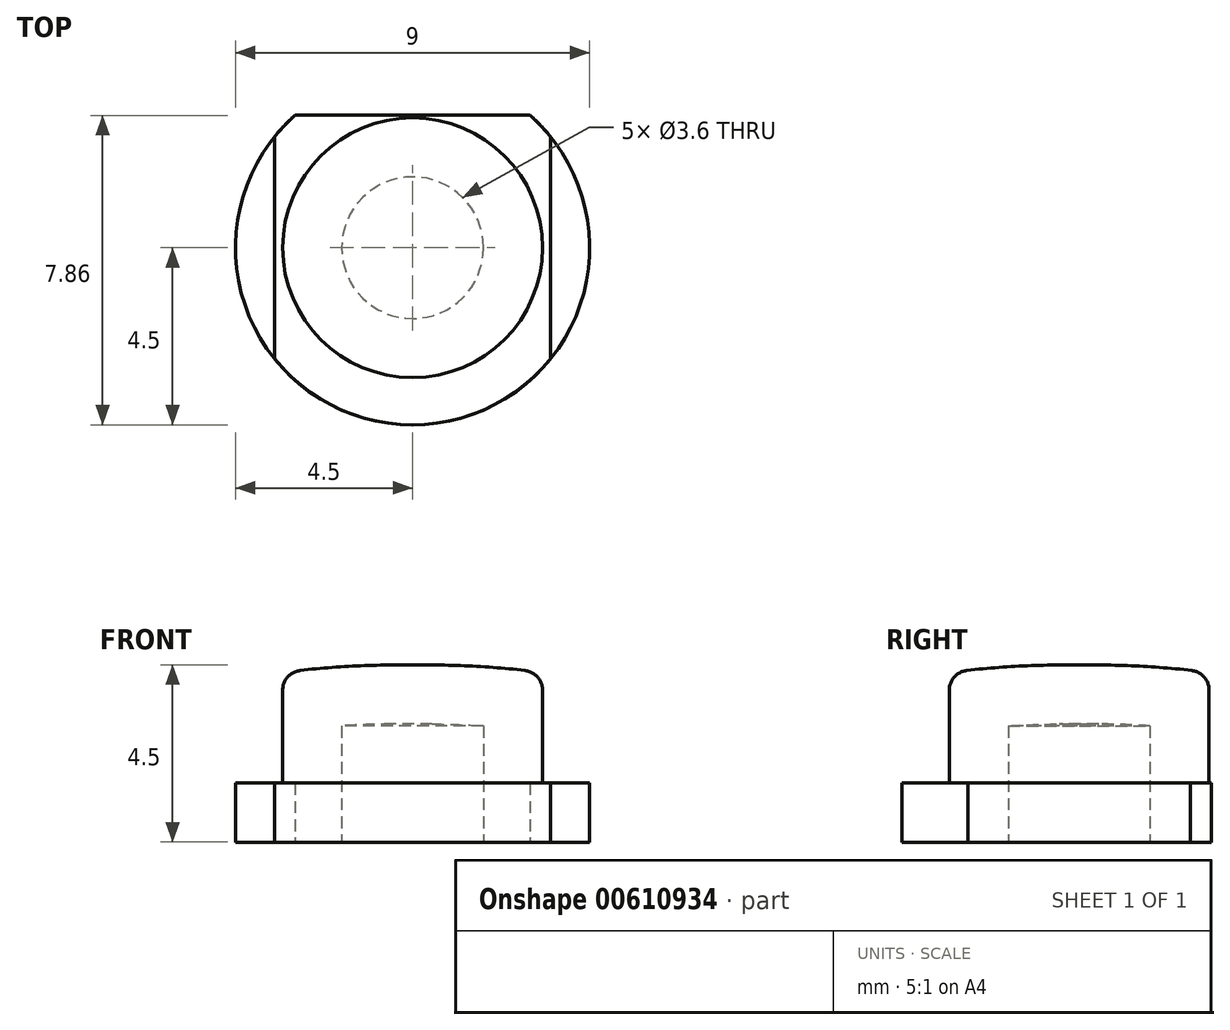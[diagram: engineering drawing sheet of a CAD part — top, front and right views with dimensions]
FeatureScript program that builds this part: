
annotation { "Feature Type Name" : "Feature", "Feature Type Description" : "" }
export const myFeature = defineFeature(function(context is Context, id is Id, definition is map)
    precondition{}
    {
        {
            var Q0;
            Q0=qCreatedBy(makeId("Front.planeOp"),FACE);
            var sketch = newSketch(context, id + "F0", { "sketchPlane" : qUnion([Q0])});
            skLineSegment(sketch, "E0", {"start": v(0, -0.55) * mm, "end": v(0, 3.95) * mm});
            skLineSegment(sketch, "E1", {"start": v(3.3, 3.75) * mm, "end": v(3.3, 0.95) * mm});
            skLineSegment(sketch, "E2", {"start": v(3.3, 0.95) * mm, "end": v(4.5, 0.95) * mm});
            skLineSegment(sketch, "E3", {"start": v(4.5, 0.95) * mm, "end": v(4.5, -0.55) * mm});
            skLineSegment(sketch, "E4", {"start": v(4.5, -0.55) * mm, "end": v(0, -0.55) * mm});
            skLineSegment(sketch, "E5", {"start": v(0, 3.95) * mm, "end": v(0.5, 3.95) * mm});
            skArc(sketch, "E6", {"start": v(3.3, 3.75) * mm, "mid": v(1.9, 3.9) * mm, "end": v(0.5, 3.95) * mm});
            skSolve(sketch);
        }
        {
            var Q0;
            Q0=qSketchRegion(id+"F0",true);
            var Q1;
            Q1=sQuery(id+"F0.wireOp",EDGE,"E0");
            revolve(context, id + "F1", {"entities" : qUnion([Q0]), "axis" : qUnion([Q1]), "revolveType" : RevolveType.FULL});
        }
        {
            var Q0;
            Q0=makeQuery(id+"F1.opRevolve","SWEPT_EDGE",EDGE,{"disambiguationData":[OSD([sQuery(id+"F0.wireOp",EDGE,"E1"),sQuery(id+"F0.wireOp",EDGE,"E6")])]});
            fillet(context, id + "F2", {"entities" : qUnion([Q0]), "radius" : 0.5 * mm, "tangentPropagation" : true, "allowEdgeOverflow" : false});
        }
        {
            var Q0;
            Q0=makeQuery(id+"F1.opRevolve","SWEPT_FACE",FACE,{"disambiguationData":[OSD([sQuery(id+"F0.wireOp",EDGE,"E4")])]});
            shell(context, id + "F3", {"entities" : qUnion([Q0]), "thickness" : 1.5 * mm});
        }
        {
            var Q0;
            Q0=makeQuery(id+"F1.opRevolve","SWEPT_BODY",BODY,{"disambiguationData":[OSD([sQuery(id+"F0.wireOp",EDGE,"E0"),sQuery(id+"F0.wireOp",EDGE,"E1"),sQuery(id+"F0.wireOp",EDGE,"E2"),sQuery(id+"F0.wireOp",EDGE,"E3"),sQuery(id+"F0.wireOp",EDGE,"E4"),sQuery(id+"F0.wireOp",EDGE,"E5"),sQuery(id+"F0.wireOp",EDGE,"E6")])]});
            transform(context, id + "F4", {"entities" : qUnion([Q0]), "transformType" : TransformType.COPY});
        }
        {
            var Q0;
            Q0=qCreatedBy(makeId("Top.planeOp"),FACE);
            var sketch = newSketch(context, id + "F5", { "sketchPlane" : qUnion([Q0])});
            skLineSegment(sketch, "E7.bottom", {"start": v(3.5, 7.34) * mm, "end": v(6.77, 7.34) * mm});
            skLineSegment(sketch, "E7.top", {"start": v(3.5, -6.74) * mm, "end": v(6.77, -6.74) * mm});
            skLineSegment(sketch, "E7.left", {"start": v(3.5, 7.34) * mm, "end": v(3.5, -6.74) * mm});
            skLineSegment(sketch, "E7.right", {"start": v(6.77, 7.34) * mm, "end": v(6.77, -6.74) * mm});
            skSolve(sketch);
        }
        {
            var Q0;
            Q0=qSketchRegion(id+"F5",true);
            extrude(context, id + "F6", {"entities" : qUnion([Q0]), "operationType" : NewBodyOperationType.REMOVE, "endBound" : BoundingType.SYMMETRIC, "oppositeDirection" : true, "depth" : 25 * mm, "offsetDistance" : 25 * mm});
        }
        {
            var Q0;
            Q0=makeQuery(id+"F4.opPattern","COPY",BODY,{"derivedFrom":makeQuery(id+"F1.opRevolve","SWEPT_BODY",BODY,{"disambiguationData":[OSD([sQuery(id+"F0.wireOp",EDGE,"E0"),sQuery(id+"F0.wireOp",EDGE,"E1"),sQuery(id+"F0.wireOp",EDGE,"E2"),sQuery(id+"F0.wireOp",EDGE,"E3"),sQuery(id+"F0.wireOp",EDGE,"E4"),sQuery(id+"F0.wireOp",EDGE,"E5"),sQuery(id+"F0.wireOp",EDGE,"E6")])]}),"instanceName":"1"});
            var Q1;
            Q1=qCreatedBy(makeId("Right.planeOp"),FACE);
            mirror(context, id + "F7", {"entities" : qUnion([Q0]), "mirrorPlane" : qUnion([Q1])});
        }
        {
            var Q0;
            Q0=makeQuery(id+"F4.opPattern","COPY",BODY,{"derivedFrom":makeQuery(id+"F1.opRevolve","SWEPT_BODY",BODY,{"disambiguationData":[OSD([sQuery(id+"F0.wireOp",EDGE,"E0"),sQuery(id+"F0.wireOp",EDGE,"E1"),sQuery(id+"F0.wireOp",EDGE,"E2"),sQuery(id+"F0.wireOp",EDGE,"E3"),sQuery(id+"F0.wireOp",EDGE,"E4"),sQuery(id+"F0.wireOp",EDGE,"E5"),sQuery(id+"F0.wireOp",EDGE,"E6")])]}),"instanceName":"1"});
            var Q1;
            Q1=makeQuery(id+"F7.opPattern","COPY",BODY,{"derivedFrom":makeQuery(id+"F4.opPattern","COPY",BODY,{"derivedFrom":makeQuery(id+"F1.opRevolve","SWEPT_BODY",BODY,{"disambiguationData":[OSD([sQuery(id+"F0.wireOp",EDGE,"E0"),sQuery(id+"F0.wireOp",EDGE,"E1"),sQuery(id+"F0.wireOp",EDGE,"E2"),sQuery(id+"F0.wireOp",EDGE,"E3"),sQuery(id+"F0.wireOp",EDGE,"E4"),sQuery(id+"F0.wireOp",EDGE,"E5"),sQuery(id+"F0.wireOp",EDGE,"E6")])]}),"instanceName":"1"}),"instanceName":"1"});
            transform(context, id + "F8", {"entities" : qUnion([Q0, Q1]), "transformType" : TransformType.COPY});
        }
        {
            var Q0;
            Q0=qCreatedBy(makeId("Top.planeOp"),FACE);
            var sketch = newSketch(context, id + "F9", { "sketchPlane" : qUnion([Q0])});
            skLineSegment(sketch, "E8.bottom", {"start": v(-6.07, 5.42) * mm, "end": v(5.37, 5.42) * mm});
            skLineSegment(sketch, "E8.top", {"start": v(-6.07, 3.36) * mm, "end": v(5.37, 3.36) * mm});
            skLineSegment(sketch, "E8.left", {"start": v(-6.07, 5.42) * mm, "end": v(-6.07, 3.36) * mm});
            skLineSegment(sketch, "E8.right", {"start": v(5.37, 5.42) * mm, "end": v(5.37, 3.36) * mm});
            skSolve(sketch);
        }
        {
            var Q0;
            Q0=qSketchRegion(id+"F9",true);
            extrude(context, id + "F10", {"entities" : qUnion([Q0]), "operationType" : NewBodyOperationType.REMOVE, "endBound" : BoundingType.SYMMETRIC, "oppositeDirection" : true, "depth" : 25 * mm, "offsetDistance" : 25 * mm});
        }
    });
